AUTODESK INVENTOR PART (.ipt)
format: ipt  version: 2017 (Build 210142000, 142)  size: 152,064 bytes
history: native  units: mm
features: extrude x9, sketch x8, other x3, projected_geometry x3, fillet x2
ambient origin geometry x8: Origin, YZ Plane, XZ Plane, XY Plane, X Axis, Y Axis, Z Axis, Center Point
bodies: Solid1 (feature_tree)
feature tree (25):
  other  "Table"
  other  "PowerPoint240V"
  other  "PowerPoint400V"
  extrude  "Extrusion1"  Depth=60.0mm
  extrude  "Extrusion2"  Depth=47.0mm
  extrude  "Extrusion3"  Depth=45.0mm
  extrude  "Extrusion240V1"  Depth=44.0mm TaperAngle=0.0deg
  fillet  "Fillet240V1"  Radius=2.5mm
  extrude  "Extrusion240V2"  Depth=5.0mm
  extrude  "Extrusion240V3"  Depth=10.0mm TaperAngle=0.0deg
  extrude  "Extrusion400V1"  Depth=15.0mm
  fillet  "Fillet400V1"  Radius=5.0mm
  extrude  "Extrusion400V2"  Depth=2.5mm
  extrude  "Extrusion400V3"  Depth=10.0mm TaperAngle=0.0deg
  sketch  "Sketch1"  dims[d0=60.0mm d1=60.0mm]
  sketch  "Sketch2"  dims[d2=10.0mm d3=0.0mm d4=47.0mm]
  sketch  "Sketch3"  dims[d5=34.0mm d6=0.0mm d7=45.0mm]
  projected_geometry  "Projected Loop1"
  sketch  "Sketch4"  dims[d8=5.0mm d9=44.0mm d10=0.0mm d11=2.5mm]
  projected_geometry  "Projected Loop2"
  projected_geometry  "Projected Loop3"
  sketch  "Sketch6"  dims[d12=10.0mm d13=0.0mm d14=5.0mm]
  sketch  "Sketch7"  dims[d15=15.0mm d16=10.0mm d17=0.0mm]
  sketch  "Sketch8"  dims[d18=30.0mm d19=15.0mm d20=5.0mm d21=0.0mm]
  sketch  "Sketch9"  dims[d22=0.0mm d28=2.5mm d29=10.0mm d30=0.0mm d31=5.0mm d32=15.0mm d33=10.0mm d34=0.0mm d35=30.0mm d36=15.0mm d38=5.0mm d39=0.0mm]
